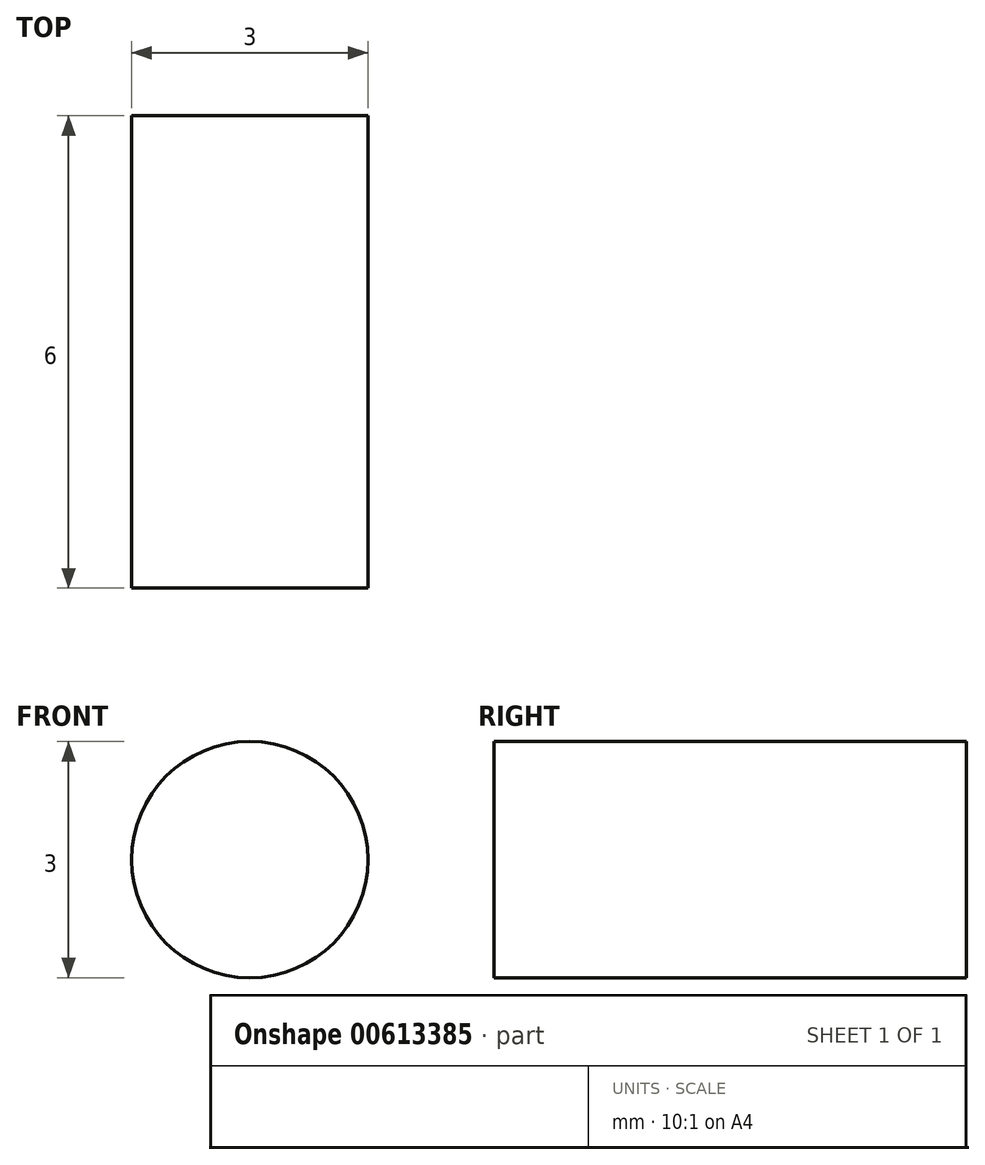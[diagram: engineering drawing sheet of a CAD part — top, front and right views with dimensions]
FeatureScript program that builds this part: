
annotation { "Feature Type Name" : "Feature", "Feature Type Description" : "" }
export const myFeature = defineFeature(function(context is Context, id is Id, definition is map)
    precondition{}
    {
        {
            var Q0;
            Q0=qCreatedBy(makeId("Front.planeOp"),FACE);
            var sketch = newSketch(context, id + "F0", { "sketchPlane" : qUnion([Q0])});
            skCircle(sketch, "E0", {"center": v(0, 0) * mm, "radius": 1.5 * mm});
            skSolve(sketch);
        }
        {
            var Q0;
            Q0=makeQuery(id+"F0.imprint","IMPRINT",FACE,{"disambiguationData":[TD([[makeQuery(id+"F0.imprint","IMPRINT",EDGE,{"derivedFrom":sQuery(id+"F0.wireOp",EDGE,"E0")}),1.0]])]});
            extrude(context, id + "F1", {"entities" : qUnion([Q0]), "depth" : 6 * mm, "offsetDistance" : 25 * mm});
        }
    });
